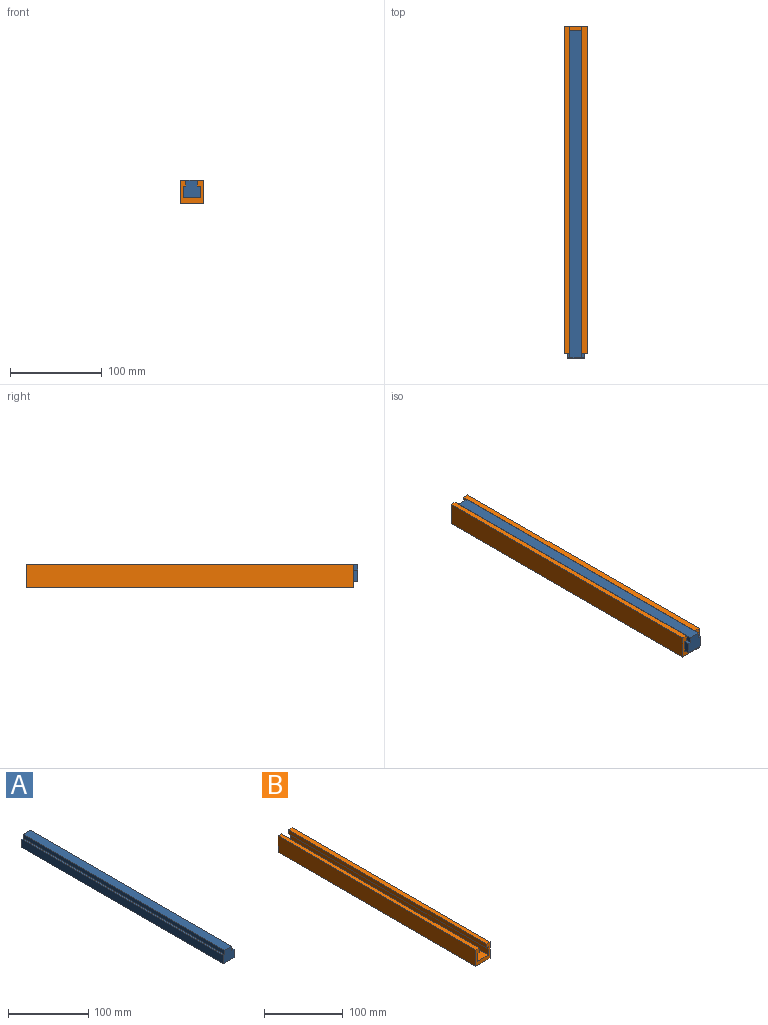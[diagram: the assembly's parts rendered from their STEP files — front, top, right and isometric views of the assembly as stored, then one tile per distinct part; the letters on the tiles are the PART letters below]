
ASSEMBLY  parts=2 mates=1
PART A: 10 faces, bbox 19.1x355.6x19.1 mm
  f0: plane 355.6x2.79mm, normal (0,0,1), area 993.5mm2, adj f1,f7,f8,f9
  f1: plane 355.6x12.7mm, normal (-1,0,0), area 4516.1mm2, adj f0,f2,f8,f9
  f2: plane 355.6x19.05mm, normal (0,0,-1), area 6774.2mm2, adj f1,f3,f8,f9
  f3: plane 355.6x12.7mm, normal (1,0,0), area 4516.1mm2, adj f2,f4,f8,f9
  f4: plane 355.6x3.56mm, normal (0,0,1), area 1264.5mm2, adj f3,f5,f8,f9
  f5: plane 355.6x6.35mm, normal (1,0,0), area 2258.1mm2, adj f4,f6,f8,f9
  f6: plane 355.6x12.7mm, normal (0,0,1), area 4516.1mm2, adj f5,f7,f8,f9
  f7: plane 355.6x6.35mm, normal (-1,0,0), area 2258.1mm2, adj f0,f6,f8,f9
  f8: plane 19.05x19.05mm, normal (0,-1,0), area 322.6mm2, adj f0,f1,f2,f3,f4,f5,f6,f7
  f9: plane 19.05x19.05mm, normal (0,1,0), area 322.6mm2, adj f0,f1,f2,f3,f4,f5,f6,f7
PART B: 14 faces, bbox 25.4x355.6x25.4 mm
  f0: plane 355.6x3.55mm, normal (0,0,-1), area 1263.7mm2, adj f1,f11,f12,f13
  f1: plane 355.6x12.7mm, normal (-1,0,0), area 4516.1mm2, adj f0,f2,f12,f13
  f2: plane 355.6x19.05mm, normal (0,0,1), area 6774.2mm2, adj f1,f3,f12,f13
  f3: plane 355.6x12.7mm, normal (1,0,0), area 4516.1mm2, adj f2,f4,f12,f13
  f4: plane 355.6x2.8mm, normal (0,0,-1), area 994.4mm2, adj f3,f5,f12,f13
  f5: plane 355.6x6.35mm, normal (1,0,0), area 2258.1mm2, adj f4,f6,f12,f13
  f6: plane 355.6x5.97mm, normal (0,0,1), area 2123.4mm2, adj f5,f7,f12,f13
  f7: plane 355.6x25.4mm, normal (-1,0,0), area 9032.2mm2, adj f6,f8,f12,f13
  f8: plane 355.6x25.4mm, normal (0,0,-1), area 9032.2mm2, adj f7,f9,f12,f13
  f9: plane 355.6x25.4mm, normal (1,0,0), area 9032.2mm2, adj f8,f10,f12,f13
  f10: plane 355.6x6.73mm, normal (0,0,1), area 2392.7mm2, adj f9,f11,f12,f13
  f11: plane 355.6x6.35mm, normal (-1,0,0), area 2258.1mm2, adj f0,f10,f12,f13
  f12: plane 25.4x25.4mm, normal (0,-1,0), area 322.6mm2, adj f0,f1,f2,f3,f4,f5,f6,f7
  f13: plane 25.4x25.4mm, normal (0,1,0), area 322.6mm2, adj f0,f1,f2,f3,f4,f5,f6,f7
PLACE A t=(23.15,-7.23,-55.96)mm
PLACE B t=(29.88,-1.83,-62.31)mm
MATE slider A.f8 <-> B.f12  axis (0,-1,0) through (29.88,-362.83,-68.66)mm
